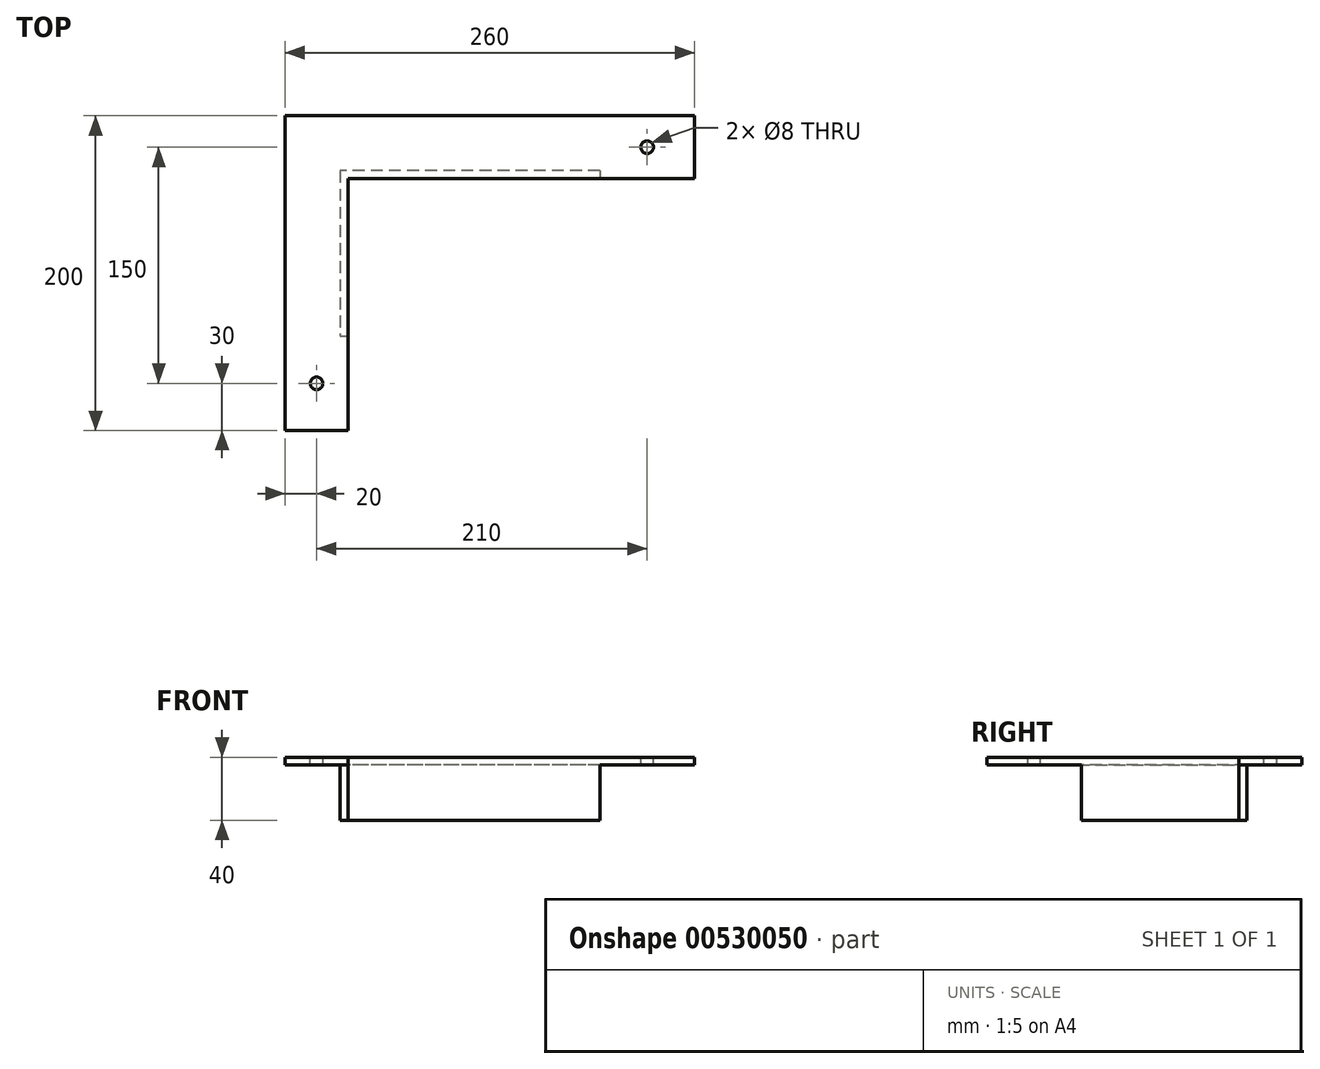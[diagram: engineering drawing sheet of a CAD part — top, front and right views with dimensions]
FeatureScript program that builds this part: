
annotation { "Feature Type Name" : "Feature", "Feature Type Description" : "" }
export const myFeature = defineFeature(function(context is Context, id is Id, definition is map)
    precondition{}
    {
        {
            var Q0;
            Q0=qCreatedBy(makeId("Top.planeOp"),FACE);
            var sketch = newSketch(context, id + "F0", { "sketchPlane" : qUnion([Q0])});
            skLineSegment(sketch, "E0.bottom", {"start": v(130, -20) * mm, "end": v(-130, -20) * mm});
            skLineSegment(sketch, "E0.top", {"start": v(130, 20) * mm, "end": v(-130, 20) * mm});
            skLineSegment(sketch, "E0.left", {"start": v(130, -20) * mm, "end": v(130, 20) * mm});
            skLineSegment(sketch, "E0.right", {"start": v(-130, -20) * mm, "end": v(-130, 20) * mm});
            skPoint(sketch, "E0.middle", {"position": v(0, 0) * mm});
            skSolve(sketch);
        }
        {
            var Q0;
            Q0=makeQuery(id+"F0.imprint","IMPRINT",FACE,{"disambiguationData":[TD([[makeQuery(id+"F0.imprint","IMPRINT",EDGE,{"derivedFrom":sQuery(id+"F0.wireOp",EDGE,"E0.bottom")}),-1.0]])]});
            extrude(context, id + "F1", {"entities" : qUnion([Q0]), "depth" : 5 * mm, "offsetDistance" : 25 * mm});
        }
        {
            var Q0;
            Q0=makeQuery(id+"F1.opExtrude","CAP_FACE",FACE,{"disambiguationData":[OSD([sQuery(id+"F0.wireOp",EDGE,"E0.bottom"),sQuery(id+"F0.wireOp",EDGE,"E0.top"),sQuery(id+"F0.wireOp",EDGE,"E0.left"),sQuery(id+"F0.wireOp",EDGE,"E0.right")])],"isStart":true});
            var sketch = newSketch(context, id + "F2", { "sketchPlane" : qUnion([Q0])});
            skLineSegment(sketch, "E1", {"start": v(130, 20) * mm, "end": v(70, 20) * mm});
            skLineSegment(sketch, "E2", {"start": v(70, 15) * mm, "end": v(70, 20) * mm});
            skLineSegment(sketch, "E3", {"start": v(70, 15) * mm, "end": v(-90, 15) * mm});
            skLineSegment(sketch, "E4", {"start": v(-90, 15) * mm, "end": v(-90, 20) * mm});
            skSolve(sketch);
        }
        {
            var Q0;
            Q0 = qSketchRegion(id + "F2", true);
            var Q1;
            {var subQ0=sQuery(id+"F2.wireOp",EDGE,"E2");Q1=makeQuery(id+"F2.imprint","IMPRINT",FACE,{"disambiguationData":[TD([[makeQuery(id+"F2.imprint","IMPRINT",EDGE,{"derivedFrom":subQ0}),1.0]])]});}
            extrude(context, id + "F3", {"entities" : qUnion([Q0, Q1]), "operationType" : NewBodyOperationType.ADD, "depth" : 35 * mm, "offsetDistance" : 25 * mm});
        }
        {
            var Q0;
            Q0=makeQuery(id+"F1.opExtrude","CAP_FACE",FACE,{"disambiguationData":[OSD([sQuery(id+"F0.wireOp",EDGE,"E0.bottom"),sQuery(id+"F0.wireOp",EDGE,"E0.top"),sQuery(id+"F0.wireOp",EDGE,"E0.left"),sQuery(id+"F0.wireOp",EDGE,"E0.right")])],"isStart":true});
            var sketch = newSketch(context, id + "F4", { "sketchPlane" : qUnion([Q0])});
            skLineSegment(sketch, "E5", {"start": v(-130, 20) * mm, "end": v(-130, 180) * mm});
            skLineSegment(sketch, "E6", {"start": v(-130, 180) * mm, "end": v(-90, 180) * mm});
            skLineSegment(sketch, "E7", {"start": v(-90, 180) * mm, "end": v(-90, 20) * mm});
            skSolve(sketch);
        }
        {
            var Q0;
            Q0 = qSketchRegion(id + "F4", true);
            var Q1;
            Q1=makeQuery(id+"F4.imprint","IMPRINT",FACE,{"disambiguationData":[TD([[makeQuery(id+"F4.imprint","IMPRINT",EDGE,{"derivedFrom":sQuery(id+"F4.wireOp",EDGE,"E5")}),-1.0]])]});
            extrude(context, id + "F5", {"entities" : qUnion([Q0, Q1]), "operationType" : NewBodyOperationType.ADD, "oppositeDirection" : true, "depth" : 5 * mm, "offsetDistance" : 25 * mm});
        }
        {
            var Q0;
            {var subQ0=sQuery(id+"F0.wireOp",EDGE,"E0.bottom");Q0=makeQuery(id+"F5.boolean.opBoolean","MERGE",FACE,{"derivedFrom":[makeQuery(id+"F1.opExtrude","CAP_FACE",FACE,{"disambiguationData":[OSD([subQ0,sQuery(id+"F0.wireOp",EDGE,"E0.top"),sQuery(id+"F0.wireOp",EDGE,"E0.left"),sQuery(id+"F0.wireOp",EDGE,"E0.right")])],"isStart":true}),makeQuery(id+"F5.opExtrude","CAP_FACE",FACE,{"disambiguationData":[OSD([subQ0,sQuery(id+"F4.wireOp",EDGE,"E5"),sQuery(id+"F4.wireOp",EDGE,"E6"),sQuery(id+"F4.wireOp",EDGE,"E7")])],"isStart":true})]});}
            var sketch = newSketch(context, id + "F6", { "sketchPlane" : qUnion([Q0])});
            skLineSegment(sketch, "E8", {"start": v(-90, 15) * mm, "end": v(-95, 15) * mm});
            skLineSegment(sketch, "E9", {"start": v(-95, 15) * mm, "end": v(-95, 120) * mm});
            skLineSegment(sketch, "E10", {"start": v(-95, 120) * mm, "end": v(-90, 120) * mm});
            skSolve(sketch);
        }
        {
            var Q0;
            Q0 = qSketchRegion(id + "F6", true);
            var Q1;
            Q1=makeQuery(id+"F6.imprint","IMPRINT",FACE,{"disambiguationData":[TD([[makeQuery(id+"F6.imprint","IMPRINT",EDGE,{"derivedFrom":sQuery(id+"F6.wireOp",EDGE,"E8")}),-1.0]])]});
            extrude(context, id + "F7", {"entities" : qUnion([Q0, Q1]), "operationType" : NewBodyOperationType.ADD, "depth" : 35 * mm, "offsetDistance" : 25 * mm});
        }
        {
            var Q0;
            {var subQ0=sQuery(id+"F0.wireOp",EDGE,"E0.bottom");Q0=makeQuery(id+"F5.boolean.opBoolean","MERGE",FACE,{"derivedFrom":[makeQuery(id+"F1.opExtrude","CAP_FACE",FACE,{"disambiguationData":[OSD([subQ0,sQuery(id+"F0.wireOp",EDGE,"E0.top"),sQuery(id+"F0.wireOp",EDGE,"E0.left"),sQuery(id+"F0.wireOp",EDGE,"E0.right")])],"isStart":false}),makeQuery(id+"F5.opExtrude","CAP_FACE",FACE,{"disambiguationData":[OSD([subQ0,sQuery(id+"F4.wireOp",EDGE,"E5"),sQuery(id+"F4.wireOp",EDGE,"E6"),sQuery(id+"F4.wireOp",EDGE,"E7")])],"isStart":false})]});}
            var sketch = newSketch(context, id + "F8", { "sketchPlane" : qUnion([Q0])});
            skCircle(sketch, "E11", {"center": v(-110, -150) * mm, "radius": 4 * mm});
            skCircle(sketch, "E12", {"center": v(100, 0) * mm, "radius": 4 * mm});
            skSolve(sketch);
        }
        {
            var Q0;
            Q0=makeQuery(id+"F8.imprint","IMPRINT",FACE,{"disambiguationData":[TD([[makeQuery(id+"F8.imprint","IMPRINT",EDGE,{"derivedFrom":sQuery(id+"F8.wireOp",EDGE,"E11")}),1.0]])]});
            var Q1;
            Q1=makeQuery(id+"F8.imprint","IMPRINT",FACE,{"disambiguationData":[TD([[makeQuery(id+"F8.imprint","IMPRINT",EDGE,{"derivedFrom":sQuery(id+"F8.wireOp",EDGE,"E12")}),1.0]])]});
            var Q2;
            Q2=sQuery(id+"F8.wireOp",EDGE,"E11");
            var Q3;
            Q3=sQuery(id+"F8.wireOp",EDGE,"E12");
            extrude(context, id + "F9", {"entities" : qUnion([Q0, Q1]), "operationType" : NewBodyOperationType.REMOVE, "surfaceEntities" : qUnion([Q2, Q3]), "oppositeDirection" : true, "depth" : 25 * mm, "offsetDistance" : 25 * mm});
        }
    });
